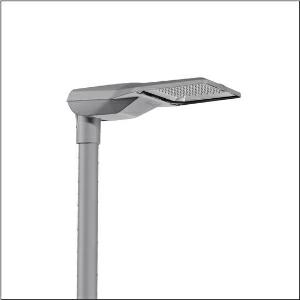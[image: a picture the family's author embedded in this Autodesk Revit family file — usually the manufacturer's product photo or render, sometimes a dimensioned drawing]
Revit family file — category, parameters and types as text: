
# Revit family: streetlight_sl_21_iq_midi___st1_5a_5xe3p41d08mb_62ad
name_source: partatom
category: Lighting Fixtures
units: mm (PartAtom-declared; Revit-internal decimal feet)

## family parameters
Cut with Voids When Loaded = No
Host = Face
Light Source = No
Part Type = Normal
Room Calculation Point = No
Round Connector Dimension = Use Diameter
Shared = No

## types (1)
- --- (1 x LED, 20000 lm, 146.7 W, 4000K)
    Apparent Load = 147 VA
    CIE Flux Codes = 22 53 95 100 100
    Color Rendering = 70
    Color Temperature = 4000K
    Default Elevation = 1800 mm
    Description = Streetlight SL 21 iQ midi, mast luminaire, primary light control with lens, of PMMA, primary optical cover: cover, of toughened safety glass, transparent, light distribution: ST1.5a, light emission: direct distribution, primary light characteristic: asymmetric, installation type: post-top, side-entry, LED, High Power LED, rated luminous flux: 20.000lm, luminous efficacy: 136lm/W, light colour: 740, colour temperature: 4000K, control: Auto-Match, Temp-Guard, Lumen-Switch, Night-Set, Smart-Wire, Light-Fading, Desk-Remote (wireless, voltage-free reading and setting of iQ features in the workshop via application-optimized NFC function/RFID function), optimised constant luminous flux control (CLO 2.0), presetting dimming linear, mains connection: 230..240V, AC, 50/60Hz, start of lifetime: 147W, end of service life: 161W, reduction: 62W, luminaire housing, of diecast aluminium, powder-coated, Siteco® metallic grey (DB 702S), corrosivity category C5 mid according to DIN EN ISO 12944, please order mast flange separately, inclination adjustable: 0°, 5°, 10°, 15°, sealing non-destructively replaceable, multi-level sealing system, length: 644mm, width: 335mm, height: 110mm, mast flange for spigot size: 42mm (side-entry): 5XC10008XM4, 60/48mm (side-entry/post-top): 5XC10108XM2, 76/60mm (side-entry/post-top): 5XC10108XM1, protection rating (complete): IP66, insulation class (complete): insulation class II (safety insulation), certification: CE, ENEC, ENEC+, VDE, impact resistance: IK09, permissible operating ambient temperature for outdoor applications: -40..+50°C, standard-compliant lighting for roads and squares, packaging unit: 1 piece

Light Distribution: ST1.5a
    Height = 111 mm
    Lamp = 1 x LED
    Lamp Light Flux = 20000 lm
    Lamp Power = 146.7 W
    Lamp count = 1
    Length = 644 mm
    Luminous efficacy = 136 lm/W
    Manufacturer = Siteco
    ModVariant = No
    Model = 5XE3P41D08MB
    Number of Poles = 1
    OnlyDefault = Yes
    Power Factor = 1
    Product Name = Streetlight SL 21 iQ midi | ST1.5a
    Product group = mast luminaire | pylon top
    ProductGroupID = 6100
    Protection Class = Protection class II
    Protection Degree = IP 66
    RLX_Detail_Level = 1
    RLX_Emergency_Light_Flux = 0 lm
    RLX_Emergency_Type = 0
    RLX_Emergency_Type_DB = No
    RlxData = <blob elided: 94201 chars, md5=1ec8ddcf>
    Socket = socket
    Standby Power = 0 W
    System Light Flux = 20000 lm
    System Power = 147 W
    Type Comments = factory setting: luminous flux: 100 % | dim-lin: 254 | 753 mA
    Type Image = l_1004298.jpg
    URL = http://relux.com
    VarID = @adj_109623
    Voltage = 0 V
    Weight = 0.00 kg
    Width = 336 mm

## geometry (parser evidence)
native form markers: Blend x4, Sweep x11
no freeform markers — native parametric forms only
